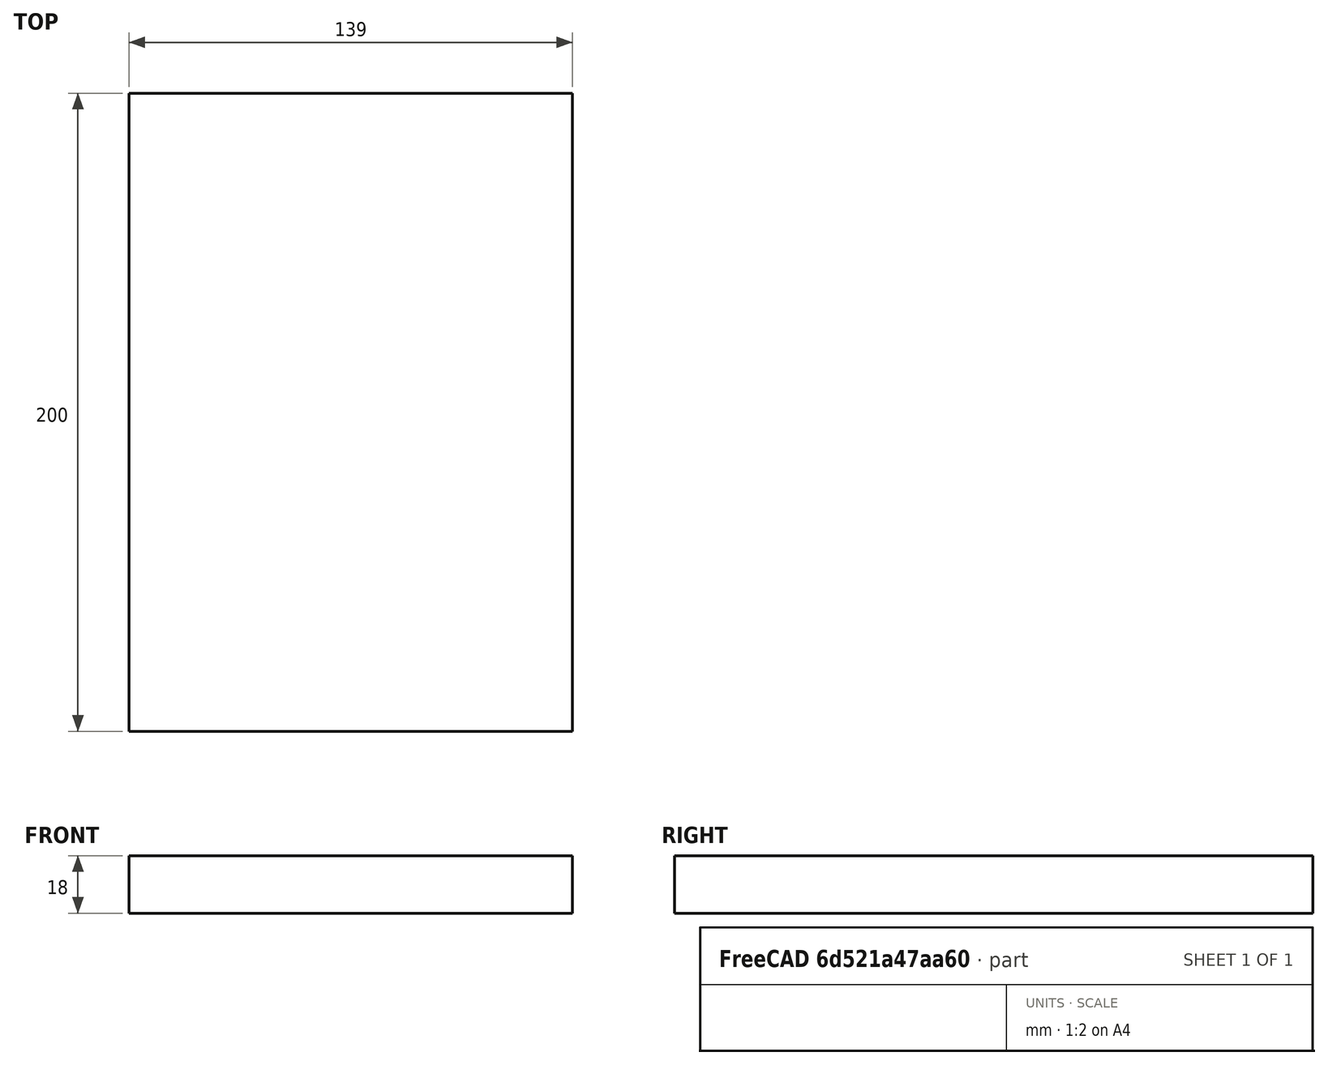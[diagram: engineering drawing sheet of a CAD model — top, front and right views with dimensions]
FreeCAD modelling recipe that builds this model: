
FCSTD DOCUMENT  (FreeCAD 1.0R39109 (Git))
Label: 32_shelf_base_short
License: All rights reserved
LicenseURL: http://en.wikipedia.org/wiki/All_rights_reserved
objects: Spreadsheet::Sheet×1, Sketcher::SketchObject×1, PartDesign::Pad×1, PartDesign::Body×1
note: 6 computed .brp shape members not serialized (recipe doc carries the construction recipe); baked Part::Feature solids carry a one-line shape summary decoded from their .brp

FEATURE [Spreadsheet::Sheet] Spreadsheet
  cells = A2='length; B2(length)=139; A3='width; B3(width)=200; A4='height; B4(height)=18
FEATURE [Sketcher::SketchObject] Sketch
  ArcFitTolerance = 0
  AttachmentSupport = -> [XY_Plane]
  FullyConstrained = true
  MakeInternals = false
  MapMode = 5
  expr: Constraints[11] = Spreadsheet.length
  expr: Constraints[12] = Spreadsheet.width
  sketch-geometry (5):
    g0: LineSegment StartX=-69.5 StartY=100 StartZ=0 EndX=69.5 EndY=100 EndZ=0
    g1: LineSegment StartX=69.5 StartY=100 StartZ=0 EndX=69.5 EndY=-100 EndZ=0
    g2: LineSegment StartX=69.5 StartY=-100 StartZ=0 EndX=-69.5 EndY=-100 EndZ=0
    g3: LineSegment StartX=-69.5 StartY=-100 StartZ=0 EndX=-69.5 EndY=100 EndZ=0
    g4: LineSegment [constr] StartX=-69.5 StartY=100 StartZ=0 EndX=69.5 EndY=-100 EndZ=0
  constraints (13):
    c: Coincident(g0,g1)
    c: Coincident(g1,g2)
    c: Coincident(g2,g3)
    c: Coincident(g3,g0)
    c: Horizontal(g0)
    c: Horizontal(g2)
    c: Vertical(g1)
    c: Vertical(g3)
    c: Coincident(g4,g1)
    c: Coincident(g0,g4)
    c: Symmetric(g0,g1,g-1)
    c: Distance(g0,g0) = 139
    c: Distance(g0,g2) = 200
FEATURE [PartDesign::Pad] Pad
  Direction = (0,0,1)
  Length = 18
  Length2 = 10
  Profile = -> Sketch
  ReferenceAxis = -> Sketch [N_Axis]
  Suppressed = false
  Type = 0
  expr: Length = Spreadsheet.height
FEATURE [PartDesign::Body] Body
  AllowCompound = false
  Group = -> [Sketch,Pad]
  Origin = -> Origin
  Tip = -> Pad
